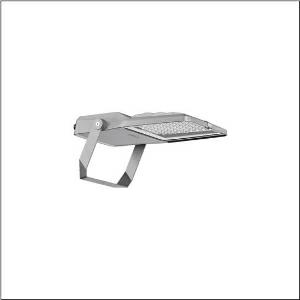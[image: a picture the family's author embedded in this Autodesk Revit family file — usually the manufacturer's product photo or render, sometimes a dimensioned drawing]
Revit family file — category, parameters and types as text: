
# Revit family: floodlight_fl_21_mini___pl52_5xa7776d2d1a_6cb1
name_source: partatom
category: Lighting Fixtures
units: mm (PartAtom-declared; Revit-internal decimal feet)

## family parameters
Cut with Voids When Loaded = No
Host = Face
Light Source = No
Part Type = Normal
Room Calculation Point = No
Round Connector Dimension = Use Diameter
Shared = No

## types (1)
- --- (1 x LED, 17840 lm, 142.9 W, 3000K)
    Apparent Load = 143 VA
    CIE Flux Codes = 26 60 98 100 100
    Color Rendering = 70
    Color Temperature = 3000K
    Default Elevation = 1800 mm
    Description = Floodlight FL 21 mini, floodlight, primary light control with lens, of PMMA, primary optical cover: protective disc, of toughened safety glass, transparent, light distribution: PL52, light emission: direct distribution, installation type: surface-mounted, LED, High Power LED, rated luminous flux: 17.840lm, luminous efficacy: 125lm/W, light colour: 730, colour temperature: 3000K, control gear: Smart Interface (Zhaga), control: flexible luminous flux parameterisation, time-dependent luminous flux control, constant luminous flux control, overheat protection, pre-setting: logarithmic dimming characteristic, with terminal, 6-pole, mains connection: 220..240V, AC, 50/60Hz, start of lifetime: 143W, end of service life: 151W, reduction: 63W, luminaire housing, of diecast aluminium, powder-coated, Siteco® metallic grey (DB 702S), corrosivity category C5 mid according to DIN EN ISO 12944, suitable for swimming pools, chlorine-resistant, sealing non-destructively replaceable, mounting bracket, of steel, galvanised, powder-coated, Siteco® metallic grey (DB 702S), Smart Interface below and above, protection rating (complete): IP66, insulation class (complete): insulation class II (safety insulation), certification: CE, ENEC, VDE, protection symbol: D, impact resistance: IK08, permissible operating ambient temperature: -40..+40°C, permissible operating ambient temperature for outdoor applications: -40..+50°C, standard: DIN EN 12944, LABS conformity tested according to VDMA 24364:2018-05, packaging unit: 1 piece

Light Distribution: PL52
    Height = 70 mm
    Lamp = 1 x LED
    Lamp Light Flux = 17840 lm
    Lamp Power = 142.9 W
    Lamp count = 1
    Length = 485 mm
    Luminous efficacy = 125 lm/W
    Manufacturer = Siteco
    ModVariant = No
    Model = 5XA7776D2D1A
    Number of Poles = 1
    OnlyDefault = Yes
    Power Factor = 1
    Product Name = Floodlight FL 21 mini | PL52
    Product group = floodlight | pylon annexe
    ProductGroupID = 6201
    Protection Class = Protection class II
    Protection Degree = IP 66
    RLX_Detail_Level = 1
    RLX_Emergency_Light_Flux = 0 lm
    RLX_Emergency_Type = 0
    RLX_Emergency_Type_DB = No
    RlxData = <blob elided: 96449 chars, md5=e4f2ecfc>
    Socket = socket
    Standby Power = 0 W
    System Light Flux = 17840 lm
    System Power = 143 W
    Type Comments = factory setting: luminous flux: 100 % | dim-lin: 254 | 730 mA
    Type Image = l_1006845.jpg
    URL = http://relux.com
    VarID = @adj_184599
    Voltage = 0 V
    Weight = 0.00 kg
    Width = 337 mm

## geometry (parser evidence)
native form markers: Blend x4, Sweep x11
no freeform markers — native parametric forms only
